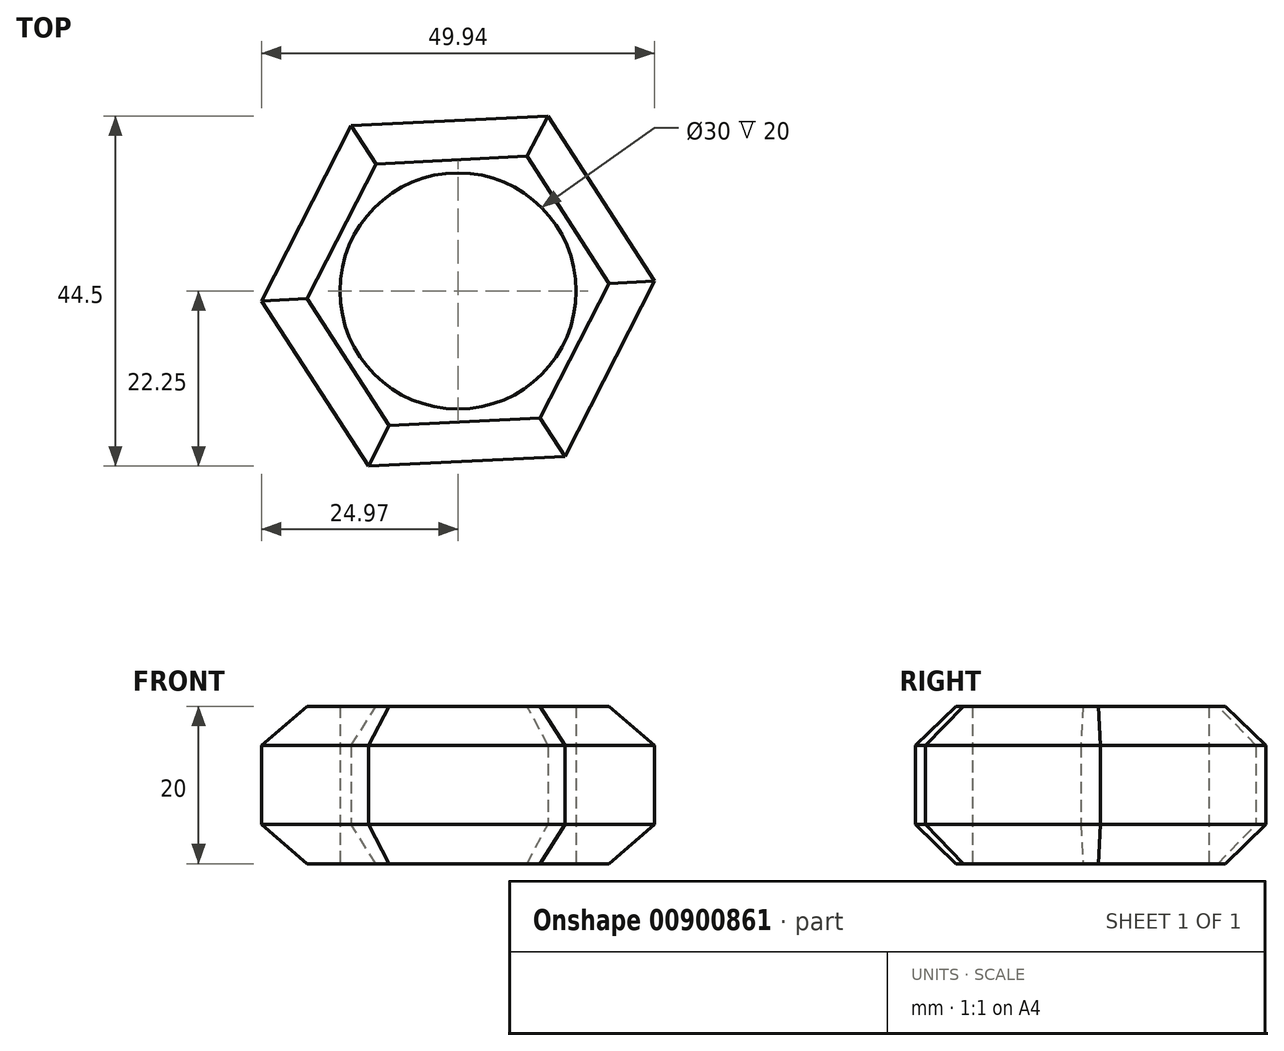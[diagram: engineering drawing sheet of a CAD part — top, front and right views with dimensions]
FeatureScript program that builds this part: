
annotation { "Feature Type Name" : "Feature", "Feature Type Description" : "" }
export const myFeature = defineFeature(function(context is Context, id is Id, definition is map)
    precondition{}
    {
        {
            var Q0;
            Q0=qCreatedBy(makeId("Top.planeOp"),FACE);
            var sketch = newSketch(context, id + "F0", { "sketchPlane" : qUnion([Q0])});
            skCircle(sketch, "E0.cCircle", {"center": v(0, 0) * mm, "radius": 25 * mm, "construction": true});
            skLineSegment(sketch, "E0.0", {"start": v(13.57, -21) * mm, "end": v(-11.4, -22.25) * mm});
            skLineSegment(sketch, "E0.1", {"start": v(-11.4, -22.25) * mm, "end": v(-24.97, -1.25) * mm});
            skLineSegment(sketch, "E0.2", {"start": v(-24.97, -1.25) * mm, "end": v(-13.57, 21) * mm});
            skLineSegment(sketch, "E0.3", {"start": v(-13.57, 21) * mm, "end": v(11.4, 22.25) * mm});
            skLineSegment(sketch, "E0.4", {"start": v(11.4, 22.25) * mm, "end": v(24.97, 1.25) * mm});
            skLineSegment(sketch, "E0.5", {"start": v(24.97, 1.25) * mm, "end": v(13.57, -21) * mm});
            skCircle(sketch, "E1", {"center": v(0, 0) * mm, "radius": 15 * mm});
            skSolve(sketch);
        }
        {
            var Q0;
            Q0=makeQuery(id+"F0.imprint","IMPRINT",FACE,{"disambiguationData":[TD([[makeQuery(id+"F0.imprint","IMPRINT",EDGE,{"derivedFrom":sQuery(id+"F0.wireOp",EDGE,"E1")}),1.0]])]});
            var Q1;
            Q1=makeQuery(id+"F0.imprint","IMPRINT",FACE,{"disambiguationData":[TD([[makeQuery(id+"F0.imprint","IMPRINT",EDGE,{"derivedFrom":sQuery(id+"F0.wireOp",EDGE,"E0.0")}),-1.0]])]});
            extrude(context, id + "F1", {"entities" : qUnion([Q0, Q1]), "depth" : 20 * mm, "offsetDistance" : 25 * mm});
        }
        {
            var Q0;
            Q0=makeQuery(id+"F1.opExtrude","CAP_FACE",FACE,{"disambiguationData":[OSD([sQuery(id+"F0.wireOp",EDGE,"E0.0"),sQuery(id+"F0.wireOp",EDGE,"E0.1"),sQuery(id+"F0.wireOp",EDGE,"E0.2"),sQuery(id+"F0.wireOp",EDGE,"E0.3"),sQuery(id+"F0.wireOp",EDGE,"E0.4"),sQuery(id+"F0.wireOp",EDGE,"E0.5")])],"isStart":true});
            var sketch = newSketch(context, id + "F2", { "sketchPlane" : qUnion([Q0])});
            skCircle(sketch, "E2", {"center": v(0, 0) * mm, "radius": 15 * mm});
            skSolve(sketch);
        }
        {
            var Q0;
            Q0 = qSketchRegion(id + "F2", true);
            extrude(context, id + "F3", {"entities" : qUnion([Q0]), "operationType" : NewBodyOperationType.REMOVE, "oppositeDirection" : true, "depth" : 33.7 * mm, "offsetDistance" : 25 * mm});
        }
        {
            var Q0;
            Q0=makeQuery(id+"F1.opExtrude","CAP_EDGE",EDGE,{"disambiguationData":[OSD([sQuery(id+"F0.wireOp",EDGE,"E0.0")])],"isStart":false});
            var Q1;
            Q1=makeQuery(id+"F1.opExtrude","CAP_EDGE",EDGE,{"disambiguationData":[OSD([sQuery(id+"F0.wireOp",EDGE,"E0.0")])],"isStart":true});
            var Q2;
            Q2=makeQuery(id+"F1.opExtrude","CAP_EDGE",EDGE,{"disambiguationData":[OSD([sQuery(id+"F0.wireOp",EDGE,"E0.1")])],"isStart":true});
            var Q3;
            Q3=makeQuery(id+"F1.opExtrude","CAP_EDGE",EDGE,{"disambiguationData":[OSD([sQuery(id+"F0.wireOp",EDGE,"E0.1")])],"isStart":false});
            var Q4;
            Q4=makeQuery(id+"F1.opExtrude","CAP_EDGE",EDGE,{"disambiguationData":[OSD([sQuery(id+"F0.wireOp",EDGE,"E0.2")])],"isStart":true});
            var Q5;
            Q5=makeQuery(id+"F1.opExtrude","CAP_EDGE",EDGE,{"disambiguationData":[OSD([sQuery(id+"F0.wireOp",EDGE,"E0.2")])],"isStart":false});
            var Q6;
            Q6=makeQuery(id+"F1.opExtrude","CAP_EDGE",EDGE,{"disambiguationData":[OSD([sQuery(id+"F0.wireOp",EDGE,"E0.3")])],"isStart":false});
            var Q7;
            Q7=makeQuery(id+"F1.opExtrude","CAP_EDGE",EDGE,{"disambiguationData":[OSD([sQuery(id+"F0.wireOp",EDGE,"E0.3")])],"isStart":true});
            var Q8;
            Q8=makeQuery(id+"F1.opExtrude","CAP_EDGE",EDGE,{"disambiguationData":[OSD([sQuery(id+"F0.wireOp",EDGE,"E0.4")])],"isStart":true});
            var Q9;
            Q9=makeQuery(id+"F1.opExtrude","CAP_EDGE",EDGE,{"disambiguationData":[OSD([sQuery(id+"F0.wireOp",EDGE,"E0.4")])],"isStart":false});
            var Q10;
            Q10=makeQuery(id+"F1.opExtrude","CAP_EDGE",EDGE,{"disambiguationData":[OSD([sQuery(id+"F0.wireOp",EDGE,"E0.5")])],"isStart":false});
            var Q11;
            Q11=makeQuery(id+"F1.opExtrude","CAP_EDGE",EDGE,{"disambiguationData":[OSD([sQuery(id+"F0.wireOp",EDGE,"E0.5")])],"isStart":true});
            chamfer(context, id + "F4", {"entities" : qUnion([Q0, Q1, Q2, Q3, Q4, Q5, Q6, Q7, Q8, Q9, Q10, Q11]), "width" : 5 * mm, "tangentPropagation" : true});
        }
    });
